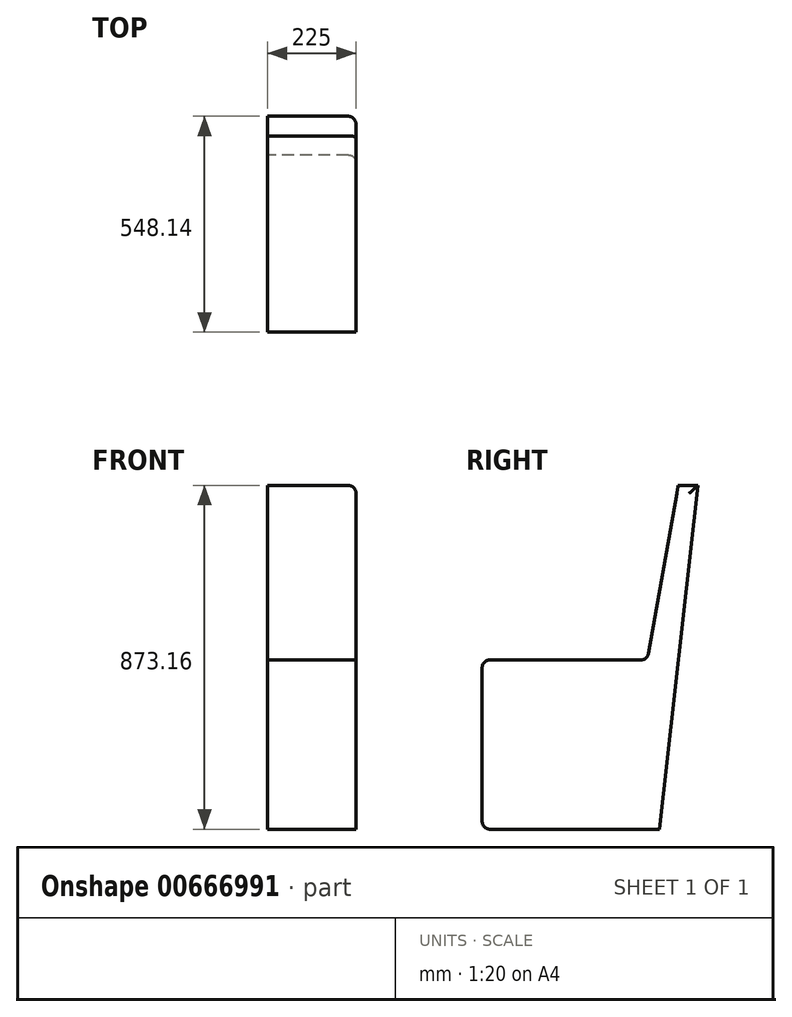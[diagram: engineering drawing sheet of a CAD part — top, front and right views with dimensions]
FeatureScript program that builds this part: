
annotation { "Feature Type Name" : "Feature", "Feature Type Description" : "" }
export const myFeature = defineFeature(function(context is Context, id is Id, definition is map)
    precondition{}
    {
        {
            var Q0;
            Q0=qCreatedBy(makeId("Right.planeOp"),FACE);
            var sketch = newSketch(context, id + "F0", { "sketchPlane" : qUnion([Q0])});
            skLineSegment(sketch, "E0", {"start": v(0, 0) * mm, "end": v(-450, 0) * mm});
            skLineSegment(sketch, "E1", {"start": v(-450, 0) * mm, "end": v(-450, 430) * mm});
            skLineSegment(sketch, "E2", {"start": v(-450, 430) * mm, "end": v(-30, 430) * mm});
            skLineSegment(sketch, "E3", {"start": v(-30, 430) * mm, "end": v(48.14, 873.16) * mm});
            skLineSegment(sketch, "E4", {"start": v(48.14, 873.16) * mm, "end": v(98.14, 873.16) * mm});
            skLineSegment(sketch, "E5", {"start": v(98.14, 873.16) * mm, "end": v(0, 0) * mm});
            skSolve(sketch);
        }
        {
            var Q0;
            Q0 = qSketchRegion(id + "F0", true);
            extrude(context, id + "F1", {"entities" : qUnion([Q0]), "depth" : 225 * mm, "offsetDistance" : 25 * mm});
        }
        {
            var Q0;
            Q0=makeQuery(id+"F1.opExtrude","SWEPT_EDGE",EDGE,{"disambiguationData":[OSD([sQuery(id+"F0.wireOp",EDGE,"E0"),sQuery(id+"F0.wireOp",EDGE,"E1")])]});
            var Q1;
            Q1=makeQuery(id+"F1.opExtrude","SWEPT_EDGE",EDGE,{"disambiguationData":[OSD([sQuery(id+"F0.wireOp",EDGE,"E1"),sQuery(id+"F0.wireOp",EDGE,"E2")])]});
            var Q2;
            Q2=makeQuery(id+"F1.opExtrude","SWEPT_EDGE",EDGE,{"disambiguationData":[OSD([sQuery(id+"F0.wireOp",EDGE,"E2"),sQuery(id+"F0.wireOp",EDGE,"E3")])]});
            var Q3;
            Q3=makeQuery(id+"F1.opExtrude","CAP_EDGE",EDGE,{"disambiguationData":[OSD([sQuery(id+"F0.wireOp",EDGE,"E4")])],"isStart":false});
            var Q4;
            Q4=makeQuery(id+"F1.opExtrude","CAP_EDGE",EDGE,{"disambiguationData":[OSD([sQuery(id+"F0.wireOp",EDGE,"E5")])],"isStart":false});
            fillet(context, id + "F2", {"entities" : qUnion([Q0, Q1, Q2, Q3, Q4]), "radius" : 20 * mm, "tangentPropagation" : true, "allowEdgeOverflow" : false});
        }
    });
